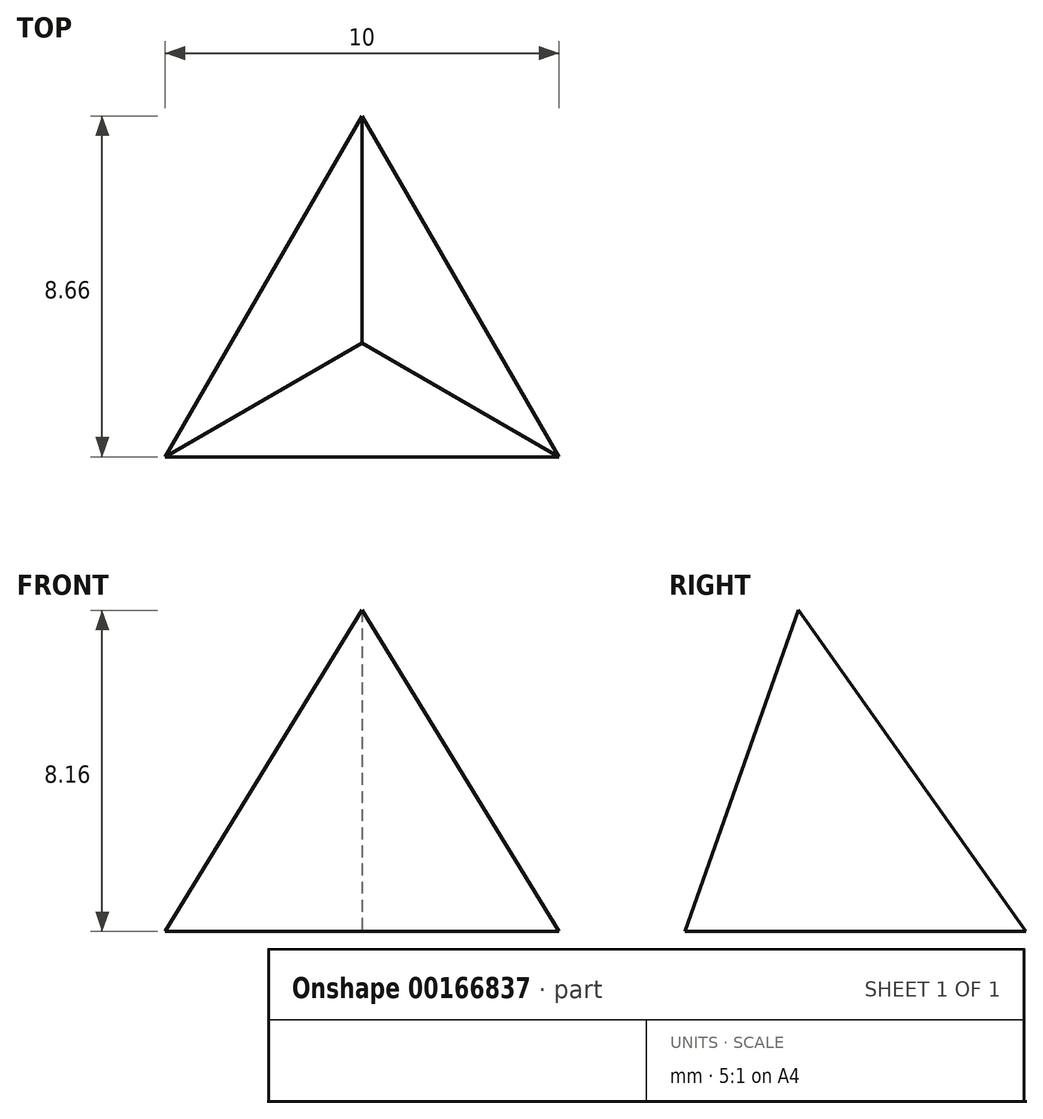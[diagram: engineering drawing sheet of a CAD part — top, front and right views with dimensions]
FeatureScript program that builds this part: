
annotation { "Feature Type Name" : "Feature", "Feature Type Description" : "" }
export const myFeature = defineFeature(function(context is Context, id is Id, definition is map)
    precondition{}
    {
        {
            var Q0;
            Q0=qCreatedBy(makeId("Top.planeOp"),FACE);
            var sketch = newSketch(context, id + "F0", { "sketchPlane" : qUnion([Q0])});
            skLineSegment(sketch, "E0", {"start": v(-5, 0) * mm, "end": v(0, 8.66) * mm});
            skLineSegment(sketch, "E1", {"start": v(0, 8.66) * mm, "end": v(5, 0) * mm});
            skLineSegment(sketch, "E2", {"start": v(5, 0) * mm, "end": v(-5, 0) * mm});
            skSolve(sketch);
        }
        {
            var Q0;
            Q0 = qSketchRegion(id + "F0", true);
            extrude(context, id + "F1", {"entities" : qUnion([Q0]), "depth" : 10 * mm, "hasDraft" : true, "draftAngle" : 90 * degree - atan(2 * (2 ^ 0.5)), "draftPullDirection" : true});
        }
    });
